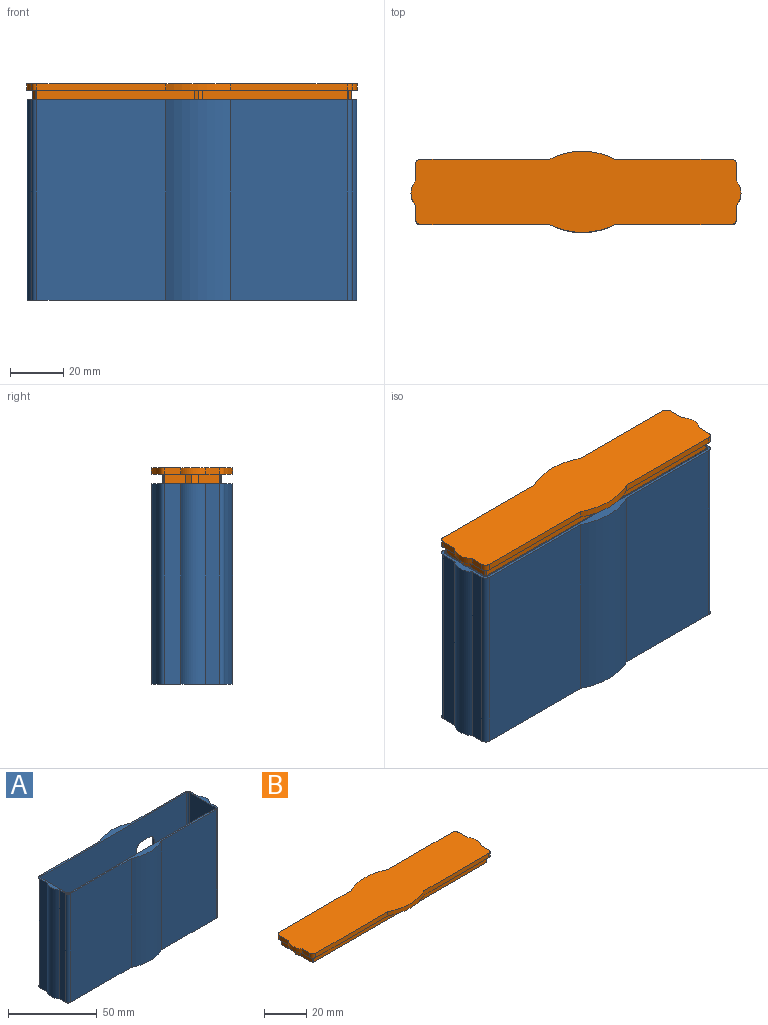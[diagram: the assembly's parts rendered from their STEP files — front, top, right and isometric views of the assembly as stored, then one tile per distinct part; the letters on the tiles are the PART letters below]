
ASSEMBLY  parts=2 mates=1
PART A: 41 faces, bbox 123.4x30.3x75 mm
  f0: plane 118x22.5mm, normal (0,0,1), area 1664.9mm2, adj f16,f17,f18,f19,f21,f22,f24,f25
  f1: cylinder r=7.23mm len=75mm, axis (0,0,-1), area 759.2mm2, adj f2,f20,f23,f32
  f2: plane 75x5.09mm, normal (-1,0,0), area 382mm2, adj f1,f3,f23,f32
  f3: cylinder r=2mm len=75mm, axis (0,0,-1), area 235.6mm2, adj f2,f4,f23,f32
  f4: plane 75x48.22mm, normal (0,-1,0), area 3616.3mm2, adj f3,f5,f23,f32
  f5: cylinder r=26.87mm len=75mm, axis (0,0,-1), area 1892.2mm2, adj f4,f6,f23,f32
  f6: plane 75x43.47mm, normal (0,-1,0), area 3260.3mm2, adj f5,f7,f23,f32
  f7: cylinder r=2mm len=75mm, axis (0,0,-1), area 235.6mm2, adj f6,f8,f23,f32
  f8: plane 75x5.09mm, normal (1,0,0), area 382mm2, adj f7,f9,f23,f32
  f9: cylinder r=7.23mm len=75mm, axis (0,0,-1), area 759.2mm2, adj f8,f10,f23,f32
  f10: plane 75x6.09mm, normal (1,0,0), area 456.8mm2, adj f9,f11,f23,f32
  f11: cylinder r=2mm len=75mm, axis (0,0,-1), area 235.6mm2, adj f10,f12,f23,f32
  f12: plane 75x43.47mm, normal (0,1,0), area 2938mm2, adj f11,f13,f23,f32,f33,f34,f35,f36
  f13: cylinder r=26.87mm len=75mm, axis (0,0,-1), area 1892.2mm2, adj f12,f14,f23,f32
  f14: plane 75x48.22mm, normal (0,1,0), area 3616.3mm2, adj f13,f15,f23,f32
  f15: cylinder r=2mm len=75mm, axis (0,0,-1), area 235.6mm2, adj f14,f20,f23,f32
  f16: plane 10x5mm, normal (1,0,0), area 50mm2, adj f0,f17,f21,f23
  f17: plane 97x5mm, normal (0,-1,0), area 485mm2, adj f0,f16,f18,f23
  f18: plane 10x5mm, normal (-1,0,0), area 50mm2, adj f0,f17,f21,f23
  f19: cylinder r=1.75mm len=5mm, axis (0,0,-1), area 55mm2, adj f0,f23
  f20: plane 75x6.09mm, normal (-1,0,0), area 456.8mm2, adj f1,f15,f23,f32
  f21: plane 97x5mm, normal (0,1,0), area 485mm2, adj f0,f16,f18,f23
  f22: cylinder r=1.75mm len=5mm, axis (0,0,-1), area 55mm2, adj f0,f23
  f23: plane 123.4x30.32mm, normal (0,0,-1), area 2064.3mm2, adj f1,f2,f3,f4,f5,f6,f7,f8
  f24: cylinder r=1mm len=70mm, axis (0,0,-1), area 110mm2, adj f0,f25,f31,f32
  f25: plane 116x70mm, normal (0,-1,0), area 7797.7mm2, adj f0,f24,f26,f32,f33,f34,f35,f36
  f26: cylinder r=1mm len=70mm, axis (0,0,-1), area 110mm2, adj f0,f25,f27,f32
  f27: plane 70x20.5mm, normal (-1,0,0), area 1435mm2, adj f0,f26,f28,f32
  f28: cylinder r=1mm len=70mm, axis (0,0,-1), area 110mm2, adj f0,f27,f29,f32
  f29: plane 116x70mm, normal (0,1,0), area 8120mm2, adj f0,f28,f30,f32
  f30: cylinder r=1mm len=70mm, axis (0,0,-1), area 110mm2, adj f0,f29,f31,f32
  f31: plane 70x20.5mm, normal (1,0,0), area 1435mm2, adj f0,f24,f30,f32
  f32: plane 123.4x30.32mm, normal (0,0,1), area 399.4mm2, adj f1,f2,f3,f4,f5,f6,f7,f8
  f33: plane 6x1mm, normal (0,0,1), area 6mm2, adj f12,f25,f34,f40
  f34: cylinder r=4mm len=4mm, axis (0,1,0), area 6.3mm2, adj f12,f25,f33,f35
  f35: plane 16x1mm, normal (1,0,0), area 16mm2, adj f12,f25,f34,f36
  f36: cylinder r=4mm len=4mm, axis (0,1,0), area 6.3mm2, adj f12,f25,f35,f37
  f37: plane 6x1mm, normal (0,0,-1), area 6mm2, adj f12,f25,f36,f38
  f38: cylinder r=4mm len=4mm, axis (0,1,0), area 6.3mm2, adj f12,f25,f37,f39
  f39: plane 16x1mm, normal (-1,0,0), area 16mm2, adj f12,f25,f38,f40
  f40: cylinder r=4mm len=4mm, axis (0,1,0), area 6.3mm2, adj f12,f25,f33,f39
PART B: 46 faces, bbox 123.4x30.3x6 mm
  f0: plane 123.43x30.35mm, normal (0,0,-1), area 532.9mm2, adj f1,f2,f3,f4,f5,f6,f7,f8
  f1: cylinder r=26.7mm len=24.3mm, axis (0,0,-1), area 63.1mm2, adj f0,f2,f16,f17
  f2: plane 43.5x2.5mm, normal (0,-1,0), area 108.7mm2, adj f0,f1,f3,f17
  f3: cylinder r=2mm len=2.5mm, axis (0,0,-1), area 7.9mm2, adj f0,f2,f4,f17
  f4: plane 5.08x2.5mm, normal (1,0,0), area 12.7mm2, adj f0,f3,f5,f17
  f5: cylinder r=7.23mm len=9.35mm, axis (0,0,-1), area 25.4mm2, adj f0,f4,f6,f17
  f6: plane 6.07x2.5mm, normal (1,0,0), area 15.2mm2, adj f0,f5,f7,f17
  f7: cylinder r=2mm len=2.5mm, axis (0,0,-1), area 7.9mm2, adj f0,f6,f8,f17
  f8: plane 43.5x2.5mm, normal (0,1,0), area 108.7mm2, adj f0,f7,f9,f17
  f9: cylinder r=26.7mm len=24.3mm, axis (0,0,-1), area 63.1mm2, adj f0,f8,f10,f17
  f10: plane 48.2x2.5mm, normal (0,1,0), area 120.5mm2, adj f0,f9,f11,f17
  f11: cylinder r=2mm len=2.5mm, axis (0,0,-1), area 7.9mm2, adj f0,f10,f12,f17
  f12: plane 6.07x2.5mm, normal (-1,0,0), area 15.2mm2, adj f0,f11,f13,f17
  f13: cylinder r=7.23mm len=9.35mm, axis (0,0,-1), area 25.4mm2, adj f0,f12,f14,f17
  f14: plane 5.08x2.5mm, normal (-1,0,0), area 12.7mm2, adj f0,f13,f15,f17
  f15: cylinder r=2mm len=2.5mm, axis (0,0,-1), area 7.9mm2, adj f0,f14,f16,f17
  f16: plane 48.2x2.5mm, normal (0,-1,0), area 120.5mm2, adj f0,f1,f15,f17
  f17: plane 123.43x30.35mm, normal (0,0,1), area 3054.3mm2, adj f1,f2,f3,f4,f5,f6,f7,f8
  f18: plane 3.5x2.46mm, normal (-0.91,-0.4,0), area 9.4mm2, adj f0,f19,f43,f44
  f19: plane 7.79x3.5mm, normal (-1,0,0), area 27.3mm2, adj f0,f18,f20,f44
  f20: cylinder r=0.5mm len=3.5mm, axis (0,0,1), area 2.7mm2, adj f0,f19,f21,f44
  f21: plane 59.04x3.5mm, normal (0,-1,0), area 206.6mm2, adj f0,f20,f22,f44
  f22: plane 3.5x1.28mm, normal (-0.23,-0.97,0), area 4.6mm2, adj f0,f21,f23,f44
  f23: cylinder r=0.5mm len=3.5mm, axis (0,0,1), area 0.8mm2, adj f0,f22,f24,f44
  f24: plane 3.5x1.42mm, normal (0.21,-0.98,0), area 5.1mm2, adj f0,f23,f25,f44
  f25: plane 54.05x3.5mm, normal (0,-1,0), area 189.2mm2, adj f0,f24,f26,f44
  f26: cylinder r=0.5mm len=3.5mm, axis (0,0,1), area 2.7mm2, adj f0,f25,f27,f44
  f27: plane 7.79x3.5mm, normal (1,0,0), area 27.3mm2, adj f0,f26,f28,f44
  f28: plane 3.5x2.46mm, normal (0.91,-0.4,0), area 9.4mm2, adj f0,f27,f29,f44
  f29: plane 3.5x2.36mm, normal (0.91,0.42,0), area 9.1mm2, adj f0,f28,f30,f44
  f30: plane 7.89x3.5mm, normal (1,0,0), area 27.6mm2, adj f0,f29,f31,f44
  f31: cylinder r=0.5mm len=3.5mm, axis (0,0,1), area 2.7mm2, adj f0,f30,f32,f44
  f32: plane 54.05x3.5mm, normal (0,1,0), area 189.2mm2, adj f0,f31,f33,f44
  f33: plane 3.5x1.42mm, normal (0.21,0.98,0), area 5.1mm2, adj f0,f32,f34,f44
  f34: cylinder r=0.5mm len=3.5mm, axis (0,0,1), area 0.8mm2, adj f0,f33,f35,f44
  f35: plane 3.5x1.28mm, normal (-0.23,0.97,0), area 4.6mm2, adj f0,f34,f36,f44
  f36: plane 59.04x3.5mm, normal (0,1,0), area 206.6mm2, adj f0,f35,f37,f44
  f37: cylinder r=0.5mm len=3.5mm, axis (0,0,1), area 2.7mm2, adj f0,f36,f38,f44
  f38: plane 7.89x3.5mm, normal (-1,0,0), area 27.6mm2, adj f0,f37,f43,f44
  f39: plane 17.5x3.5mm, normal (1,0,0), area 61.2mm2, adj f40,f42,f44,f45
  f40: plane 113x3.5mm, normal (0,-1,0), area 395.5mm2, adj f39,f41,f44,f45
  f41: plane 17.5x3.5mm, normal (-1,0,0), area 61.2mm2, adj f40,f42,f44,f45
  f42: plane 113x3.5mm, normal (0,1,0), area 395.5mm2, adj f39,f41,f44,f45
  f43: plane 3.5x2.36mm, normal (-0.91,0.42,0), area 9.1mm2, adj f0,f18,f38,f44
  f44: plane 119.18x22.12mm, normal (0,0,-1), area 544mm2, adj f18,f19,f20,f21,f22,f23,f24,f25
  f45: plane 113x17.5mm, normal (0,0,-1), area 1977.5mm2, adj f39,f40,f41,f42
PLACE A t=(-9.86,21.98,0)mm
PLACE B t=(-9.87,21.98,78.5)mm
MATE fastened A.f11 <-> B.f7  axis (0,0,1) through (116,22.5,75)mm
